# Revit family: LAMP_LUP WALL 110 DIRECT
name_source: partatom
category: Luminarias
revit_build: Autodesk Revit 2018 (Build: 20190510_1515(x64)
units: mm (PartAtom-declared; Revit-internal decimal feet)

## family parameters
Anfitrión = Cara
Compartido = No
Corte con vacíos al cargar = No
Cota de conector redondo = Diámetro de uso
Origen de luz = Sí
Punto de cálculo de habitación = No
Tipo de pieza = Normal

## types (1)
- 1295LM 4000 ASYM BLACK
    Archivo de red fotométrica = LW1110DR30AS40NB.IES
    CRI = 80
    Cambio de temperatura de color de luz atenuada = <Ninguno>
    Diameter = 110
    Efficacy = 50 lm/W
    Elevación por defecto = 1219 mm
    Filtro de color = 16777215
    Finish = Texturised black RAL 9011
    Gear = Electronic
    Height = 320
    Installation instructions = https://www.lamp.es
    Insulation class = I
    LED Lifetime = 50.000 L80 B10
    Lamp = COB LED
    Last update = 10/02/2022
    MacAdam = 3
    Manufacturer URL = http://www.lamp.es
    Manufacturer country = Spain
    Manufacturer name = LAMP
    Material COB = LAMP_COB
    Material cristal = LAMP_CRISTAL Aro Kombic
    Material cuerpo = LAMP_Aluminio perfil Ocult NG
    Material reflector = LAMP_Aluminio Reflector Imag
    Plum = 26 W
    Power = 23 W
    Power Supply = 220-240V 50/60Hz
    Product URL = https://www.lamp.es
    Product code = LW1110DR30AS40NB
    Product datasheet = http://www.lamp.es
    Protection rating = IP65 / IK06
    Type = COB PHILIPS
    Weight = 2.63 kg
    Ángulo de inclinación = 0.00°
